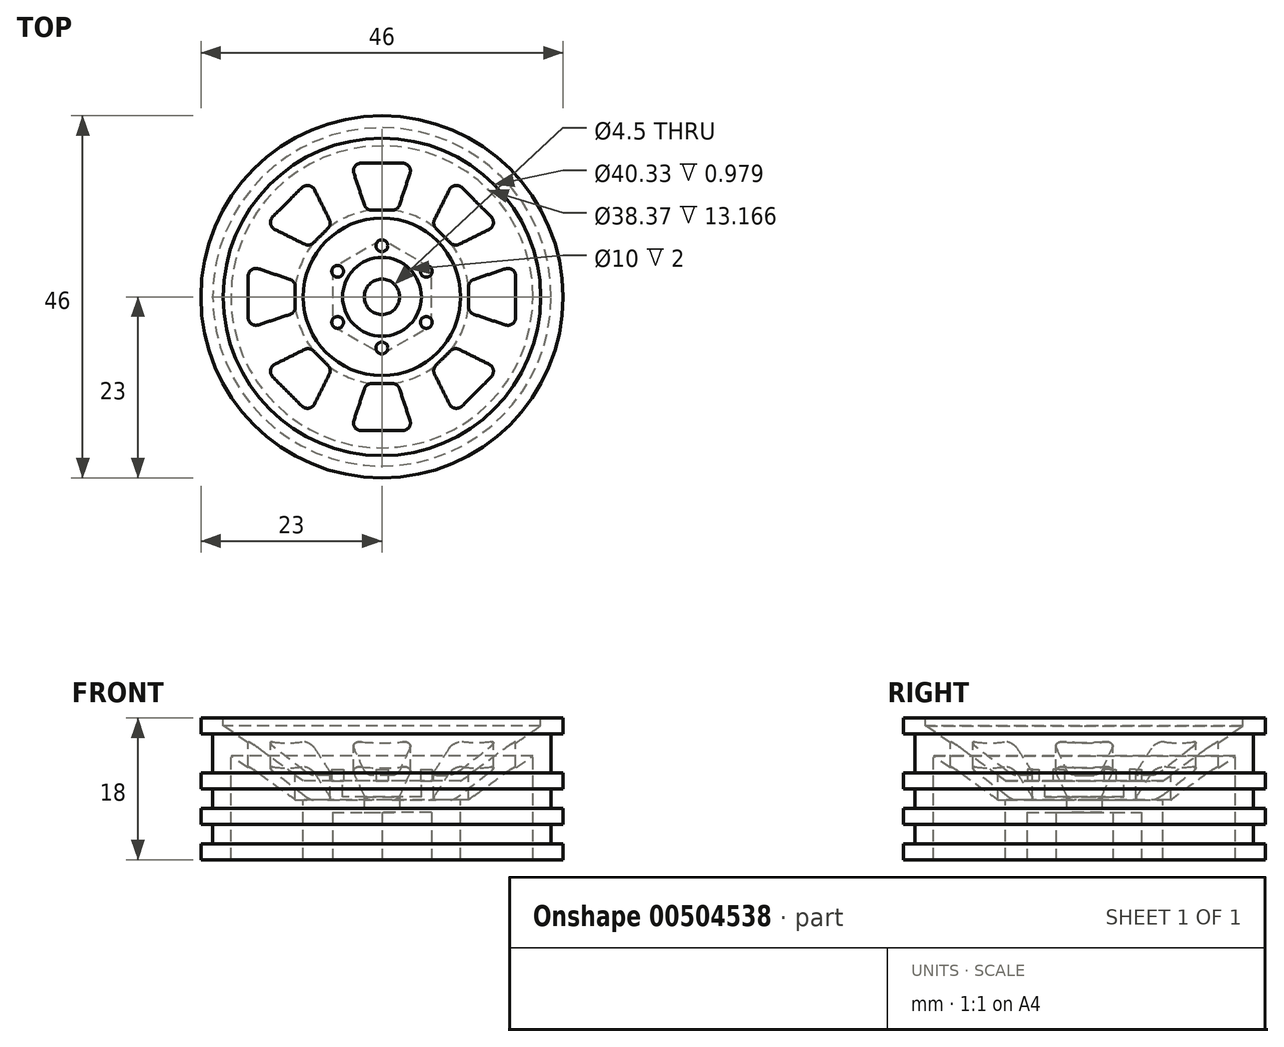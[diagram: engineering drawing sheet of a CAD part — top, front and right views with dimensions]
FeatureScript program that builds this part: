
annotation { "Feature Type Name" : "Feature", "Feature Type Description" : "" }
export const myFeature = defineFeature(function(context is Context, id is Id, definition is map)
    precondition{}
    {
        {
            var Q0;
            Q0=qCreatedBy(makeId("Front.planeOp"),FACE);
            var sketch = newSketch(context, id + "F0", { "sketchPlane" : qUnion([Q0])});
            skLineSegment(sketch, "E0", {"start": v(0, 0) * mm, "end": v(10.72, 0) * mm});
            skLineSegment(sketch, "E1", {"start": v(23, 0) * mm, "end": v(23, 2) * mm});
            skLineSegment(sketch, "E2", {"start": v(21.5, 2) * mm, "end": v(21.5, 4.5) * mm});
            skLineSegment(sketch, "E3", {"start": v(21.5, 2) * mm, "end": v(23, 2) * mm});
            skLineSegment(sketch, "E4", {"start": v(23, 4.5) * mm, "end": v(21.5, 4.5) * mm});
            skLineSegment(sketch, "E5", {"start": v(21.5, 6.5) * mm, "end": v(21.5, 9) * mm});
            skLineSegment(sketch, "E6", {"start": v(21.78, 16) * mm, "end": v(23, 16) * mm});
            skLineSegment(sketch, "E7", {"start": v(23, 16) * mm, "end": v(23, 18) * mm});
            skLineSegment(sketch, "E8", {"start": v(23, 18) * mm, "end": v(20.17, 18) * mm});
            skLineSegment(sketch, "E9", {"start": v(0, 10) * mm, "end": v(0, 0) * mm});
            skPoint(sketch, "E10.endSnap0", {"position": v(17.5, 18) * mm});
            skLineSegment(sketch, "E11", {"start": v(17.92, 15.47) * mm, "end": v(10, 10) * mm});
            skLineSegment(sketch, "E12", {"start": v(10, 10) * mm, "end": v(0, 10) * mm});
            skPoint(sketch, "E13.start.orphan", {"position": v(12, 18) * mm});
            skPoint(sketch, "E14.end.orphan", {"position": v(10.72, 0) * mm});
            skLineSegment(sketch, "E15", {"start": v(10, 6.55) * mm, "end": v(10, 0) * mm});
            skLineSegment(sketch, "E16.trimOffspring", {"start": v(19.19, 0) * mm, "end": v(23, 0) * mm});
            skLineSegment(sketch, "E17", {"start": v(23, 4.5) * mm, "end": v(23, 6.5) * mm});
            skLineSegment(sketch, "E18", {"start": v(23, 6.5) * mm, "end": v(21.5, 6.5) * mm});
            skPoint(sketch, "E19.end.orphan", {"position": v(21.5, -0.75) * mm});
            skPoint(sketch, "E20.end.orphan", {"position": v(26.5, 17) * mm});
            skPoint(sketch, "E21.end.orphan", {"position": v(23, 15) * mm});
            skLineSegment(sketch, "E22", {"start": v(21.5, 11) * mm, "end": v(23, 11) * mm});
            skLineSegment(sketch, "E23", {"start": v(23, 11) * mm, "end": v(23, 9) * mm});
            skLineSegment(sketch, "E24", {"start": v(23, 9) * mm, "end": v(21.5, 9) * mm});
            skLineSegment(sketch, "E25.trimOffspring", {"start": v(21.5, 11) * mm, "end": v(21.5, 15.72) * mm});
            skLineSegment(sketch, "E26.trimOffspring", {"start": v(21.5, 11) * mm, "end": v(21.5, 11) * mm});
            skPoint(sketch, "E27.visualSharp", {"position": v(17.5, 13.9) * mm});
            skPoint(sketch, "E28.visualSharp", {"position": v(20, 18) * mm});
            skPoint(sketch, "E29.start.orphan", {"position": v(21.5, 11) * mm});
            skPoint(sketch, "E30.visualSharp", {"position": v(21.5, 16) * mm});
            skArc(sketch, "E30.filletArc", {"start": v(21.78, 16) * mm, "mid": v(21.58, 15.92) * mm, "end": v(21.5, 15.72) * mm});
            skPoint(sketch, "E31.orphan", {"position": v(0, 21) * mm});
            skLineSegment(sketch, "E32", {"start": v(10, 10) * mm, "end": v(20.17, 17.02) * mm});
            skLineSegment(sketch, "E33", {"start": v(20.17, 18) * mm, "end": v(20.17, 17.02) * mm});
            skLineSegment(sketch, "E34", {"start": v(19.19, 12.15) * mm, "end": v(19.19, 0) * mm});
            skPoint(sketch, "E35.orphan", {"position": v(17.92, 0) * mm});
            skPoint(sketch, "E36.orphan", {"position": v(19.19, 13.9) * mm});
            skLineSegment(sketch, "E37", {"start": v(19.19, 12.15) * mm, "end": v(19.19, 13.17) * mm});
            skLineSegment(sketch, "E38", {"start": v(11.08, 7.57) * mm, "end": v(19.19, 13.17) * mm});
            skLineSegment(sketch, "E39", {"start": v(11.08, 7.57) * mm, "end": v(10, 7.57) * mm});
            skLineSegment(sketch, "E40", {"start": v(10, 6.55) * mm, "end": v(10, 7.57) * mm});
            skPoint(sketch, "E41.1.end.orphan", {"position": v(11.08, 6.55) * mm});
            skPoint(sketch, "E42.start.orphan", {"position": v(17.92, 11.28) * mm});
            skSolve(sketch);
        }
        {
            var Q0;
            Q0=makeQuery(id+"F0.imprint","IMPRINT",FACE,{"disambiguationData":[TD([[makeQuery(id+"F0.imprint","IMPRINT",EDGE,{"derivedFrom":sQuery(id+"F0.wireOp",EDGE,"E1")}),1.0]])]});
            var Q1;
            Q1=sQuery(id+"F0.wireOp",EDGE,"E9");
            revolve(context, id + "F1", {"entities" : qUnion([Q0]), "axis" : qUnion([Q1]), "revolveType" : RevolveType.FULL});
        }
        {
            var Q0;
            Q0=makeQuery(id+"F1.opRevolve","SWEPT_FACE",FACE,{"disambiguationData":[OSD([sQuery(id+"F0.wireOp",EDGE,"E8")])]});
            cPlane(context, id + "F2", {"entities" : qUnion([Q0]), "cplaneType" : CPlaneType.OFFSET, "offset" : 25 * mm, "width" : 150 * mm, "height" : 150 * mm});
        }
        {
            var Q0;
            Q0=qCreatedBy(id+"F2.planeOp",FACE);
            var sketch = newSketch(context, id + "F3", { "sketchPlane" : qUnion([Q0])});
            skLineSegment(sketch, "E43", {"start": v(-2.61, 17) * mm, "end": v(2.61, 17) * mm});
            skLineSegment(sketch, "E44", {"start": v(3.56, 15.68) * mm, "end": v(2.23, 11.68) * mm});
            skLineSegment(sketch, "E45", {"start": v(1.28, 11) * mm, "end": v(-1.28, 11) * mm});
            skLineSegment(sketch, "E46", {"start": v(-2.23, 11.68) * mm, "end": v(-3.56, 15.68) * mm});
            skPoint(sketch, "E47.visualSharp", {"position": v(-4, 17) * mm});
            skArc(sketch, "E47.filletArc", {"start": v(-2.61, 17) * mm, "mid": v(-3.42, 16.58) * mm, "end": v(-3.56, 15.68) * mm});
            skPoint(sketch, "E48.visualSharp", {"position": v(-2, 11) * mm});
            skArc(sketch, "E48.filletArc", {"start": v(-2.23, 11.68) * mm, "mid": v(-1.86, 11.19) * mm, "end": v(-1.28, 11) * mm});
            skPoint(sketch, "E49.visualSharp", {"position": v(2, 11) * mm});
            skArc(sketch, "E49.filletArc", {"start": v(1.28, 11) * mm, "mid": v(1.86, 11.19) * mm, "end": v(2.23, 11.68) * mm});
            skPoint(sketch, "E50.visualSharp", {"position": v(4, 17) * mm});
            skArc(sketch, "E50.filletArc", {"start": v(3.56, 15.68) * mm, "mid": v(3.42, 16.58) * mm, "end": v(2.61, 17) * mm});
            skLineSegment(sketch, "E51.1.0", {"start": v(-9.84, 6.69) * mm, "end": v(-13.6, 8.57) * mm});
            skLineSegment(sketch, "E51.1.1", {"start": v(-13.87, 10.17) * mm, "end": v(-10.17, 13.87) * mm});
            skLineSegment(sketch, "E51.1.2", {"start": v(-8.57, 13.6) * mm, "end": v(-6.69, 9.84) * mm});
            skLineSegment(sketch, "E51.1.3", {"start": v(-6.87, 8.68) * mm, "end": v(-8.68, 6.87) * mm});
            skArc(sketch, "E51.1.4", {"start": v(-6.87, 8.68) * mm, "mid": v(-6.6, 9.23) * mm, "end": v(-6.69, 9.84) * mm});
            skArc(sketch, "E51.1.5", {"start": v(-9.84, 6.69) * mm, "mid": v(-9.23, 6.6) * mm, "end": v(-8.68, 6.87) * mm});
            skArc(sketch, "E51.1.6", {"start": v(-8.57, 13.6) * mm, "mid": v(-9.3, 14.15) * mm, "end": v(-10.17, 13.87) * mm});
            skArc(sketch, "E51.1.7", {"start": v(-13.87, 10.17) * mm, "mid": v(-14.15, 9.3) * mm, "end": v(-13.6, 8.57) * mm});
            skLineSegment(sketch, "E51.2.0", {"start": v(-11.68, -2.23) * mm, "end": v(-15.68, -3.56) * mm});
            skLineSegment(sketch, "E51.2.1", {"start": v(-17, -2.61) * mm, "end": v(-17, 2.61) * mm});
            skLineSegment(sketch, "E51.2.2", {"start": v(-15.68, 3.56) * mm, "end": v(-11.68, 2.23) * mm});
            skLineSegment(sketch, "E51.2.3", {"start": v(-11, 1.28) * mm, "end": v(-11, -1.28) * mm});
            skArc(sketch, "E51.2.4", {"start": v(-11, 1.28) * mm, "mid": v(-11.19, 1.86) * mm, "end": v(-11.68, 2.23) * mm});
            skArc(sketch, "E51.2.5", {"start": v(-11.68, -2.23) * mm, "mid": v(-11.19, -1.86) * mm, "end": v(-11, -1.28) * mm});
            skArc(sketch, "E51.2.6", {"start": v(-15.68, 3.56) * mm, "mid": v(-16.58, 3.42) * mm, "end": v(-17, 2.61) * mm});
            skArc(sketch, "E51.2.7", {"start": v(-17, -2.61) * mm, "mid": v(-16.58, -3.42) * mm, "end": v(-15.68, -3.56) * mm});
            skLineSegment(sketch, "E51.3.0", {"start": v(-6.69, -9.84) * mm, "end": v(-8.57, -13.6) * mm});
            skLineSegment(sketch, "E51.3.1", {"start": v(-10.17, -13.87) * mm, "end": v(-13.87, -10.17) * mm});
            skLineSegment(sketch, "E51.3.2", {"start": v(-13.6, -8.57) * mm, "end": v(-9.84, -6.69) * mm});
            skLineSegment(sketch, "E51.3.3", {"start": v(-8.68, -6.87) * mm, "end": v(-6.87, -8.68) * mm});
            skArc(sketch, "E51.3.4", {"start": v(-8.68, -6.87) * mm, "mid": v(-9.23, -6.6) * mm, "end": v(-9.84, -6.69) * mm});
            skArc(sketch, "E51.3.5", {"start": v(-6.69, -9.84) * mm, "mid": v(-6.6, -9.23) * mm, "end": v(-6.87, -8.68) * mm});
            skArc(sketch, "E51.3.6", {"start": v(-13.6, -8.57) * mm, "mid": v(-14.15, -9.3) * mm, "end": v(-13.87, -10.17) * mm});
            skArc(sketch, "E51.3.7", {"start": v(-10.17, -13.87) * mm, "mid": v(-9.3, -14.15) * mm, "end": v(-8.57, -13.6) * mm});
            skLineSegment(sketch, "E51.4.0", {"start": v(2.23, -11.68) * mm, "end": v(3.56, -15.68) * mm});
            skLineSegment(sketch, "E51.4.1", {"start": v(2.61, -17) * mm, "end": v(-2.61, -17) * mm});
            skLineSegment(sketch, "E51.4.2", {"start": v(-3.56, -15.68) * mm, "end": v(-2.23, -11.68) * mm});
            skLineSegment(sketch, "E51.4.3", {"start": v(-1.28, -11) * mm, "end": v(1.28, -11) * mm});
            skArc(sketch, "E51.4.4", {"start": v(-1.28, -11) * mm, "mid": v(-1.86, -11.19) * mm, "end": v(-2.23, -11.68) * mm});
            skArc(sketch, "E51.4.5", {"start": v(2.23, -11.68) * mm, "mid": v(1.86, -11.19) * mm, "end": v(1.28, -11) * mm});
            skArc(sketch, "E51.4.6", {"start": v(-3.56, -15.68) * mm, "mid": v(-3.42, -16.58) * mm, "end": v(-2.61, -17) * mm});
            skArc(sketch, "E51.4.7", {"start": v(2.61, -17) * mm, "mid": v(3.42, -16.58) * mm, "end": v(3.56, -15.68) * mm});
            skLineSegment(sketch, "E51.5.0", {"start": v(9.84, -6.69) * mm, "end": v(13.6, -8.57) * mm});
            skLineSegment(sketch, "E51.5.1", {"start": v(13.87, -10.17) * mm, "end": v(10.17, -13.87) * mm});
            skLineSegment(sketch, "E51.5.2", {"start": v(8.57, -13.6) * mm, "end": v(6.69, -9.84) * mm});
            skLineSegment(sketch, "E51.5.3", {"start": v(6.87, -8.68) * mm, "end": v(8.68, -6.87) * mm});
            skArc(sketch, "E51.5.4", {"start": v(6.87, -8.68) * mm, "mid": v(6.6, -9.23) * mm, "end": v(6.69, -9.84) * mm});
            skArc(sketch, "E51.5.5", {"start": v(9.84, -6.69) * mm, "mid": v(9.23, -6.6) * mm, "end": v(8.68, -6.87) * mm});
            skArc(sketch, "E51.5.6", {"start": v(8.57, -13.6) * mm, "mid": v(9.3, -14.15) * mm, "end": v(10.17, -13.87) * mm});
            skArc(sketch, "E51.5.7", {"start": v(13.87, -10.17) * mm, "mid": v(14.15, -9.3) * mm, "end": v(13.6, -8.57) * mm});
            skLineSegment(sketch, "E51.6.0", {"start": v(11.68, 2.23) * mm, "end": v(15.68, 3.56) * mm});
            skLineSegment(sketch, "E51.6.1", {"start": v(17, 2.61) * mm, "end": v(17, -2.61) * mm});
            skLineSegment(sketch, "E51.6.2", {"start": v(15.68, -3.56) * mm, "end": v(11.68, -2.23) * mm});
            skLineSegment(sketch, "E51.6.3", {"start": v(11, -1.28) * mm, "end": v(11, 1.28) * mm});
            skArc(sketch, "E51.6.4", {"start": v(11, -1.28) * mm, "mid": v(11.19, -1.86) * mm, "end": v(11.68, -2.23) * mm});
            skArc(sketch, "E51.6.5", {"start": v(11.68, 2.23) * mm, "mid": v(11.19, 1.86) * mm, "end": v(11, 1.28) * mm});
            skArc(sketch, "E51.6.6", {"start": v(15.68, -3.56) * mm, "mid": v(16.58, -3.42) * mm, "end": v(17, -2.61) * mm});
            skArc(sketch, "E51.6.7", {"start": v(17, 2.61) * mm, "mid": v(16.58, 3.42) * mm, "end": v(15.68, 3.56) * mm});
            skLineSegment(sketch, "E51.7.0", {"start": v(6.69, 9.84) * mm, "end": v(8.57, 13.6) * mm});
            skLineSegment(sketch, "E51.7.1", {"start": v(10.17, 13.87) * mm, "end": v(13.87, 10.17) * mm});
            skLineSegment(sketch, "E51.7.2", {"start": v(13.6, 8.57) * mm, "end": v(9.84, 6.69) * mm});
            skLineSegment(sketch, "E51.7.3", {"start": v(8.68, 6.87) * mm, "end": v(6.87, 8.68) * mm});
            skArc(sketch, "E51.7.4", {"start": v(8.68, 6.87) * mm, "mid": v(9.23, 6.6) * mm, "end": v(9.84, 6.69) * mm});
            skArc(sketch, "E51.7.5", {"start": v(6.69, 9.84) * mm, "mid": v(6.6, 9.23) * mm, "end": v(6.87, 8.68) * mm});
            skArc(sketch, "E51.7.6", {"start": v(13.6, 8.57) * mm, "mid": v(14.15, 9.3) * mm, "end": v(13.87, 10.17) * mm});
            skArc(sketch, "E51.7.7", {"start": v(10.17, 13.87) * mm, "mid": v(9.3, 14.15) * mm, "end": v(8.57, 13.6) * mm});
            skPoint(sketch, "E51.center", {"position": v(0, 0) * mm});
            skSolve(sketch);
        }
        {
            var Q0;
            Q0=makeQuery(id+"F3.imprint","IMPRINT",FACE,{"disambiguationData":[TD([[makeQuery(id+"F3.imprint","IMPRINT",EDGE,{"derivedFrom":sQuery(id+"F3.wireOp",EDGE,"E43")}),-1.0]])]});
            var Q1;
            Q1=makeQuery(id+"F3.imprint","IMPRINT",FACE,{"disambiguationData":[TD([[makeQuery(id+"F3.imprint","IMPRINT",EDGE,{"derivedFrom":sQuery(id+"F3.wireOp",EDGE,"E51.1.0")}),-1.0]])]});
            var Q2;
            Q2=makeQuery(id+"F3.imprint","IMPRINT",FACE,{"disambiguationData":[TD([[makeQuery(id+"F3.imprint","IMPRINT",EDGE,{"derivedFrom":sQuery(id+"F3.wireOp",EDGE,"E51.2.0")}),-1.0]])]});
            var Q3;
            Q3=makeQuery(id+"F3.imprint","IMPRINT",FACE,{"disambiguationData":[TD([[makeQuery(id+"F3.imprint","IMPRINT",EDGE,{"derivedFrom":sQuery(id+"F3.wireOp",EDGE,"E51.3.0")}),-1.0]])]});
            var Q4;
            Q4=makeQuery(id+"F3.imprint","IMPRINT",FACE,{"disambiguationData":[TD([[makeQuery(id+"F3.imprint","IMPRINT",EDGE,{"derivedFrom":sQuery(id+"F3.wireOp",EDGE,"E51.4.0")}),-1.0]])]});
            var Q5;
            Q5=makeQuery(id+"F3.imprint","IMPRINT",FACE,{"disambiguationData":[TD([[makeQuery(id+"F3.imprint","IMPRINT",EDGE,{"derivedFrom":sQuery(id+"F3.wireOp",EDGE,"E51.5.0")}),-1.0]])]});
            var Q6;
            Q6=makeQuery(id+"F3.imprint","IMPRINT",FACE,{"disambiguationData":[TD([[makeQuery(id+"F3.imprint","IMPRINT",EDGE,{"derivedFrom":sQuery(id+"F3.wireOp",EDGE,"E51.6.0")}),-1.0]])]});
            var Q7;
            Q7=makeQuery(id+"F3.imprint","IMPRINT",FACE,{"disambiguationData":[TD([[makeQuery(id+"F3.imprint","IMPRINT",EDGE,{"derivedFrom":sQuery(id+"F3.wireOp",EDGE,"E51.7.0")}),-1.0]])]});
            extrude(context, id + "F4", {"entities" : qUnion([Q0, Q1, Q2, Q3, Q4, Q5, Q6, Q7]), "operationType" : NewBodyOperationType.REMOVE, "endBound" : BoundingType.THROUGH_ALL, "oppositeDirection" : true, "depth" : 25 * mm});
        }
        {
            var Q0;
            Q0=makeQuery(id+"F1.opRevolve","SWEPT_FACE",FACE,{"disambiguationData":[OSD([sQuery(id+"F0.wireOp",EDGE,"E12")])]});
            var sketch = newSketch(context, id + "F5", { "sketchPlane" : qUnion([Q0])});
            skCircle(sketch, "E52", {"center": v(0, 6.5) * mm, "radius": 0.75 * mm});
            skCircle(sketch, "E53.1.0", {"center": v(-5.63, 3.25) * mm, "radius": 0.75 * mm});
            skCircle(sketch, "E53.2.0", {"center": v(-5.63, -3.25) * mm, "radius": 0.75 * mm});
            skCircle(sketch, "E53.3.0", {"center": v(0, -6.5) * mm, "radius": 0.75 * mm});
            skCircle(sketch, "E53.4.0", {"center": v(5.63, -3.25) * mm, "radius": 0.75 * mm});
            skCircle(sketch, "E53.5.0", {"center": v(5.63, 3.25) * mm, "radius": 0.75 * mm});
            skPoint(sketch, "E53.center", {"position": v(0, 0) * mm});
            skSolve(sketch);
        }
        {
            var Q0;
            Q0=makeQuery(id+"F5.imprint","IMPRINT",FACE,{"disambiguationData":[TD([[makeQuery(id+"F5.imprint","IMPRINT",EDGE,{"derivedFrom":sQuery(id+"F5.wireOp",EDGE,"E52")}),1.0]])]});
            var Q1;
            Q1=makeQuery(id+"F5.imprint","IMPRINT",FACE,{"disambiguationData":[TD([[makeQuery(id+"F5.imprint","IMPRINT",EDGE,{"derivedFrom":sQuery(id+"F5.wireOp",EDGE,"E53.1.0")}),1.0]])]});
            var Q2;
            Q2=makeQuery(id+"F5.imprint","IMPRINT",FACE,{"disambiguationData":[TD([[makeQuery(id+"F5.imprint","IMPRINT",EDGE,{"derivedFrom":sQuery(id+"F5.wireOp",EDGE,"E53.2.0")}),1.0]])]});
            var Q3;
            Q3=makeQuery(id+"F5.imprint","IMPRINT",FACE,{"disambiguationData":[TD([[makeQuery(id+"F5.imprint","IMPRINT",EDGE,{"derivedFrom":sQuery(id+"F5.wireOp",EDGE,"E53.3.0")}),1.0]])]});
            var Q4;
            Q4=makeQuery(id+"F5.imprint","IMPRINT",FACE,{"disambiguationData":[TD([[makeQuery(id+"F5.imprint","IMPRINT",EDGE,{"derivedFrom":sQuery(id+"F5.wireOp",EDGE,"E53.4.0")}),1.0]])]});
            var Q5;
            Q5=makeQuery(id+"F5.imprint","IMPRINT",FACE,{"disambiguationData":[TD([[makeQuery(id+"F5.imprint","IMPRINT",EDGE,{"derivedFrom":sQuery(id+"F5.wireOp",EDGE,"E53.5.0")}),1.0]])]});
            extrude(context, id + "F6", {"entities" : qUnion([Q0, Q1, Q2, Q3, Q4, Q5]), "operationType" : NewBodyOperationType.ADD, "depth" : 1.5 * mm});
        }
        {
            var Q0;
            Q0=makeQuery(id+"F1.opRevolve","SWEPT_FACE",FACE,{"disambiguationData":[OSD([sQuery(id+"F0.wireOp",EDGE,"E0")])]});
            var sketch = newSketch(context, id + "F7", { "sketchPlane" : qUnion([Q0])});
            skCircle(sketch, "E54.cCircle", {"center": v(0, 0) * mm, "radius": 6.3 * mm, "construction": true});
            skLineSegment(sketch, "E54.0", {"start": v(6.3, -3.64) * mm, "end": v(0, -7.27) * mm});
            skLineSegment(sketch, "E54.1", {"start": v(0, -7.27) * mm, "end": v(-6.3, -3.64) * mm});
            skLineSegment(sketch, "E54.2", {"start": v(-6.3, -3.64) * mm, "end": v(-6.3, 3.64) * mm});
            skLineSegment(sketch, "E54.3", {"start": v(-6.3, 3.64) * mm, "end": v(0, 7.27) * mm});
            skLineSegment(sketch, "E54.4", {"start": v(0, 7.27) * mm, "end": v(6.3, 3.64) * mm});
            skLineSegment(sketch, "E54.5", {"start": v(6.3, 3.64) * mm, "end": v(6.3, -3.64) * mm});
            skPoint(sketch, "E54.0.midPoint", {"position": v(3.15, -5.46) * mm});
            skSolve(sketch);
        }
        {
            var Q0;
            Q0=makeQuery(id+"F7.imprint","IMPRINT",FACE,{"disambiguationData":[TD([[makeQuery(id+"F7.imprint","IMPRINT",EDGE,{"derivedFrom":sQuery(id+"F7.wireOp",EDGE,"E54.0")}),-1.0]])]});
            extrude(context, id + "F8", {"entities" : qUnion([Q0]), "operationType" : NewBodyOperationType.REMOVE, "oppositeDirection" : true, "depth" : 6 * mm});
        }
        {
            var Q0;
            Q0=makeQuery(id+"F8.boolean.opBoolean","COPY",FACE,{"derivedFrom":makeQuery(id+"F8.opExtrude","CAP_FACE",FACE,{"disambiguationData":[OSD([sQuery(id+"F7.wireOp",EDGE,"E54.0"),sQuery(id+"F7.wireOp",EDGE,"E54.1"),sQuery(id+"F7.wireOp",EDGE,"E54.2"),sQuery(id+"F7.wireOp",EDGE,"E54.3"),sQuery(id+"F7.wireOp",EDGE,"E54.4"),sQuery(id+"F7.wireOp",EDGE,"E54.5")])],"isStart":false})});
            var sketch = newSketch(context, id + "F9", { "sketchPlane" : qUnion([Q0])});
            skCircle(sketch, "E55", {"center": v(0, 0) * mm, "radius": 2.25 * mm});
            skSolve(sketch);
        }
        {
            var Q0;
            Q0=makeQuery(id+"F9.imprint","IMPRINT",FACE,{"disambiguationData":[TD([[makeQuery(id+"F9.imprint","IMPRINT",EDGE,{"derivedFrom":sQuery(id+"F9.wireOp",EDGE,"E55")}),1.0]])]});
            extrude(context, id + "F10", {"entities" : qUnion([Q0]), "operationType" : NewBodyOperationType.ADD, "depth" : 25 * mm});
        }
        {
            var Q0;
            Q0=makeQuery(id+"F10.opExtrude","CAP_FACE",FACE,{"disambiguationData":[OSD([sQuery(id+"F9.wireOp",EDGE,"E55")])],"isStart":false});
            extrude(context, id + "F11", {"entities" : qUnion([Q0]), "operationType" : NewBodyOperationType.REMOVE, "endBound" : BoundingType.THROUGH_ALL, "oppositeDirection" : true, "depth" : 25 * mm});
        }
        {
            var Q0;
            Q0=makeQuery(id+"F1.opRevolve","SWEPT_FACE",FACE,{"disambiguationData":[OSD([sQuery(id+"F0.wireOp",EDGE,"E12")])]});
            var sketch = newSketch(context, id + "F12", { "sketchPlane" : qUnion([Q0])});
            skCircle(sketch, "E56", {"center": v(0, 0) * mm, "radius": 5 * mm});
            skSolve(sketch);
        }
        {
            var Q0;
            Q0=makeQuery(id+"F12.imprint","IMPRINT",FACE,{"disambiguationData":[TD([[makeQuery(id+"F12.imprint","IMPRINT",EDGE,{"derivedFrom":sQuery(id+"F12.wireOp",EDGE,"E56")}),1.0]])]});
            extrude(context, id + "F13", {"entities" : qUnion([Q0]), "operationType" : NewBodyOperationType.REMOVE, "oppositeDirection" : true, "depth" : 2 * mm});
        }
    });
